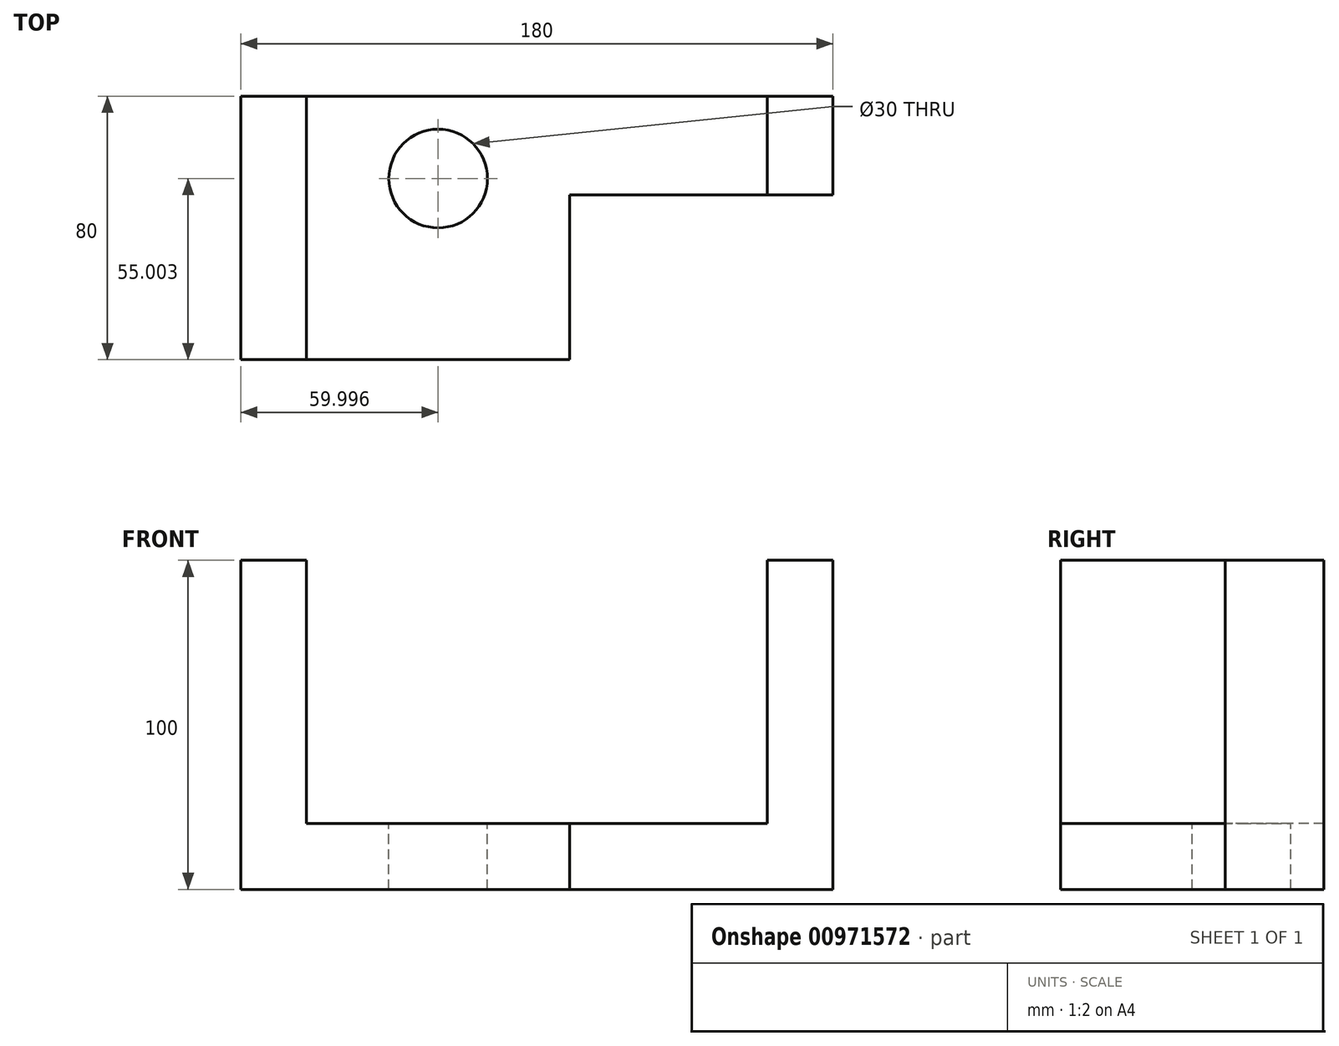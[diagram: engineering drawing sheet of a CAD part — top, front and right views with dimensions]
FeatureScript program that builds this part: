
annotation { "Feature Type Name" : "Feature", "Feature Type Description" : "" }
export const myFeature = defineFeature(function(context is Context, id is Id, definition is map)
    precondition{}
    {
        {
            var Q0;
            Q0=qCreatedBy(makeId("Top.planeOp"),FACE);
            var sketch = newSketch(context, id + "F0", { "sketchPlane" : qUnion([Q0])});
            skLineSegment(sketch, "E0.bottom", {"start": v(-48.01, 39.81) * mm, "end": v(131.99, 39.81) * mm});
            skLineSegment(sketch, "E0.top", {"start": v(-48.01, -40.19) * mm, "end": v(131.99, -40.19) * mm});
            skLineSegment(sketch, "E0.left", {"start": v(-48.01, 39.81) * mm, "end": v(-48.01, -40.19) * mm});
            skLineSegment(sketch, "E0.right", {"start": v(131.99, 39.81) * mm, "end": v(131.99, -40.19) * mm});
            skLineSegment(sketch, "E1.bottom", {"start": v(131.99, -40.19) * mm, "end": v(51.99, -40.19) * mm});
            skLineSegment(sketch, "E1.top", {"start": v(131.99, 9.81) * mm, "end": v(51.99, 9.81) * mm});
            skLineSegment(sketch, "E1.left", {"start": v(131.99, -40.19) * mm, "end": v(131.99, 9.81) * mm});
            skLineSegment(sketch, "E1.right", {"start": v(51.99, -40.19) * mm, "end": v(51.99, 9.81) * mm});
            skLineSegment(sketch, "E2.bottom", {"start": v(-48.01, 39.81) * mm, "end": v(-28.01, 39.81) * mm});
            skLineSegment(sketch, "E2.top", {"start": v(-48.01, -40.19) * mm, "end": v(-28.01, -40.19) * mm});
            skLineSegment(sketch, "E2.right", {"start": v(-28.01, 39.81) * mm, "end": v(-28.01, -40.19) * mm});
            skLineSegment(sketch, "E3.bottom", {"start": v(131.99, 39.81) * mm, "end": v(111.99, 39.81) * mm});
            skLineSegment(sketch, "E3.top", {"start": v(131.99, 9.81) * mm, "end": v(111.99, 9.81) * mm});
            skLineSegment(sketch, "E3.left", {"start": v(131.99, 39.81) * mm, "end": v(131.99, 9.81) * mm});
            skLineSegment(sketch, "E3.right", {"start": v(111.99, 39.81) * mm, "end": v(111.99, 9.81) * mm});
            skSolve(sketch);
        }
        {
            var Q0;
            {var subQ0=sQuery(id+"F0.wireOp",EDGE,"E1.right");Q0=makeQuery(id+"F0.imprint","IMPRINT",FACE,{"disambiguationData":[TD([[makeQuery(id+"F0.imprint","IMPRINT",EDGE,{"derivedFrom":subQ0}),1.0]])]});}
            extrude(context, id + "F1", {"entities" : qUnion([Q0]), "depth" : 20 * mm, "offsetDistance" : 25 * mm});
        }
        {
            var Q0;
            {var subQ2=sQuery(id+"F0.wireOp",EDGE,"E0.left");Q0=makeQuery(id+"F0.imprint","IMPRINT",FACE,{"disambiguationData":[TD([[makeQuery(id+"F0.imprint","IMPRINT",EDGE,{"derivedFrom":subQ2}),1.0]])]});}
            var Q1;
            {var subQ0=sQuery(id+"F0.wireOp",EDGE,"E3.right");Q1=makeQuery(id+"F0.imprint","IMPRINT",FACE,{"disambiguationData":[TD([[makeQuery(id+"F0.imprint","IMPRINT",EDGE,{"derivedFrom":subQ0}),1.0]])]});}
            extrude(context, id + "F2", {"entities" : qUnion([Q0, Q1]), "operationType" : NewBodyOperationType.ADD, "depth" : 100 * mm, "offsetDistance" : 25 * mm});
        }
        {
            var Q0;
            Q0=makeQuery(id+"F1.opExtrude","CAP_FACE",FACE,{"disambiguationData":[OSD([sQuery(id+"F0.wireOp",EDGE,"E0.bottom"),sQuery(id+"F0.wireOp",EDGE,"E0.top"),sQuery(id+"F0.wireOp",EDGE,"E1.top"),sQuery(id+"F0.wireOp",EDGE,"E1.right"),sQuery(id+"F0.wireOp",EDGE,"E2.right"),sQuery(id+"F0.wireOp",EDGE,"E3.right")])],"isStart":false});
            var sketch = newSketch(context, id + "F3", { "sketchPlane" : qUnion([Q0])});
            skPoint(sketch, "E4", {"position": v(11.99, 14.81) * mm});
            skSolve(sketch);
        }
        {
            var Q0;
            Q0=sQuery(id+"F3.wireOp",VERTEX,"E4");
            var Q1;
            Q1=makeQuery(id+"F1.opExtrude","SWEPT_BODY",BODY,{"disambiguationData":[OSD([sQuery(id+"F0.wireOp",EDGE,"E0.bottom"),sQuery(id+"F0.wireOp",EDGE,"E0.top"),sQuery(id+"F0.wireOp",EDGE,"E1.top"),sQuery(id+"F0.wireOp",EDGE,"E1.right"),sQuery(id+"F0.wireOp",EDGE,"E2.right"),sQuery(id+"F0.wireOp",EDGE,"E3.right")])]});
            hole(context, id + "F4", {"style" : HoleStyle.SIMPLE, "endStyle" : HoleEndStyle.THROUGH, "holeDiameter" : 30 * mm, "majorDiameter" : 5 * mm, "isTappedThrough" : true, "tappedDepth" : 12 * mm, "tapClearance" : 3, "locations" : qUnion([Q0]), "scope" : qUnion([Q1])});
        }
    });
